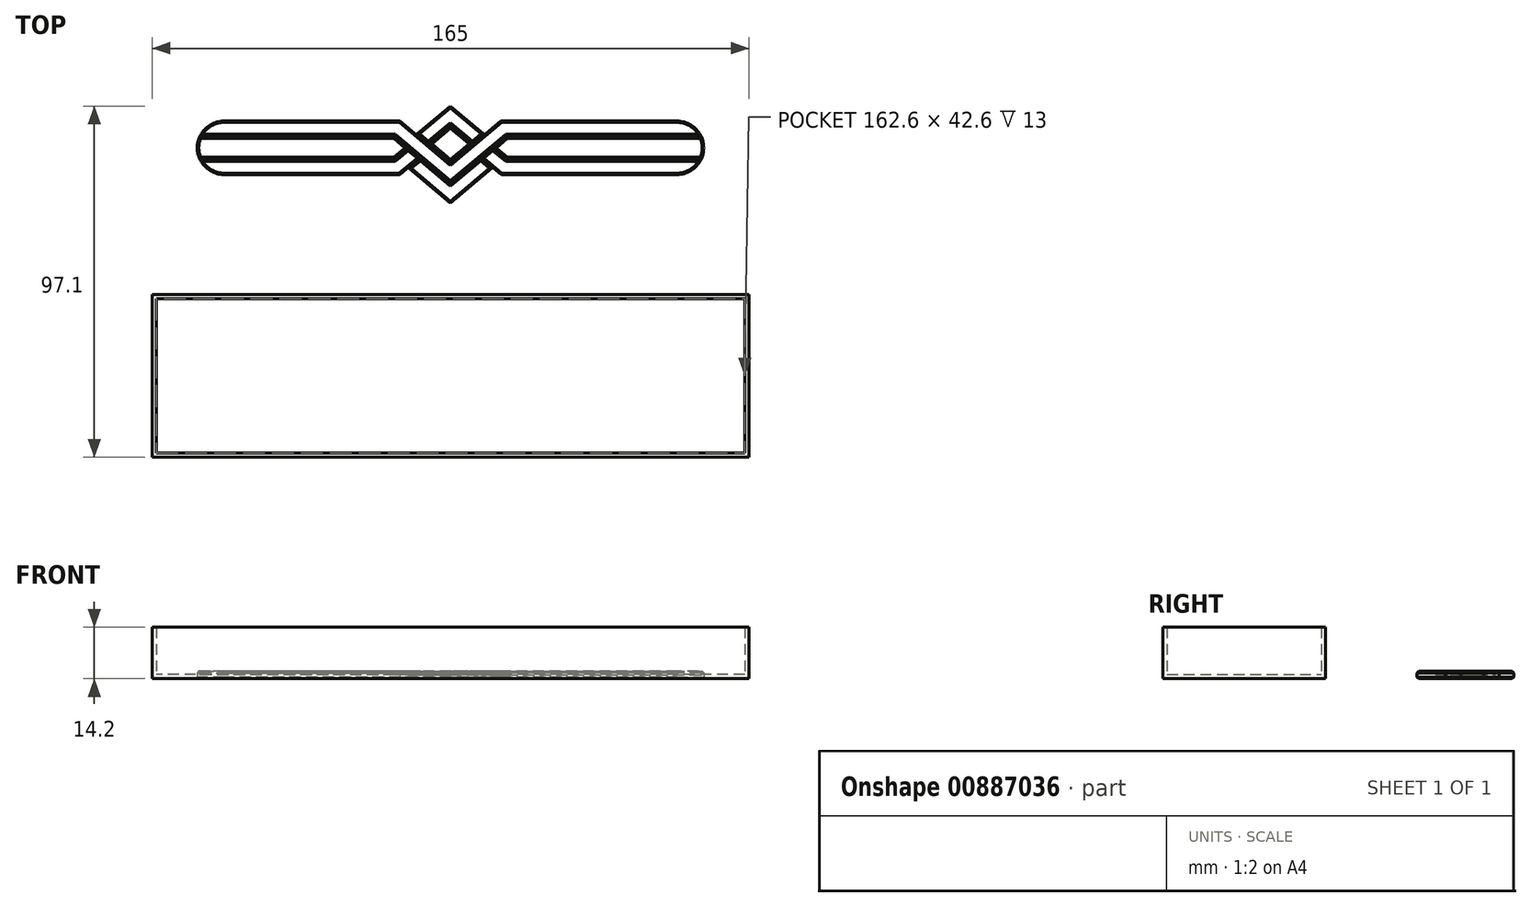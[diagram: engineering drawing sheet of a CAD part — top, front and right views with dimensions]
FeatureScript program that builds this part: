
annotation { "Feature Type Name" : "Feature", "Feature Type Description" : "" }
export const myFeature = defineFeature(function(context is Context, id is Id, definition is map)
    precondition{}
    {
        {
            var Q0;
            Q0=qCreatedBy(makeId("Top.planeOp"),FACE);
            var sketch = newSketch(context, id + "F0", { "sketchPlane" : qUnion([Q0])});
            skLineSegment(sketch, "E0", {"start": v(12, 0) * mm, "end": v(15.58, 3) * mm});
            skLineSegment(sketch, "E1", {"start": v(15.58, 3) * mm, "end": v(70, 3) * mm});
            skLineSegment(sketch, "E2", {"start": v(70, 3) * mm, "end": v(70, 0) * mm});
            skLineSegment(sketch, "E3.MirrorCS", {"start": v(12, 0) * mm, "end": v(15.58, -3) * mm});
            skLineSegment(sketch, "E4.MirrorCS", {"start": v(15.58, -3) * mm, "end": v(70, -3) * mm});
            skLineSegment(sketch, "E5.MirrorCS", {"start": v(70, -3) * mm, "end": v(70, 0) * mm});
            skLineSegment(sketch, "E6.MirrorCS", {"start": v(-12, 0) * mm, "end": v(-15.58, 3) * mm});
            skLineSegment(sketch, "E7.MirrorCS", {"start": v(-15.58, -3) * mm, "end": v(-70, -3) * mm});
            skLineSegment(sketch, "E8.MirrorCS", {"start": v(-12, 0) * mm, "end": v(-15.58, -3) * mm});
            skLineSegment(sketch, "E9.MirrorCS", {"start": v(-15.58, 3) * mm, "end": v(-70, 3) * mm});
            skLineSegment(sketch, "E10.MirrorCS", {"start": v(-70, -3) * mm, "end": v(-70, 0) * mm});
            skLineSegment(sketch, "E11.MirrorCS", {"start": v(-70, 3) * mm, "end": v(-70, 0) * mm});
            skSolve(sketch);
        }
        {
            var Q0;
            Q0=qSketchRegion(id+"F0",true);
            extrude(context, id + "F1", {"entities" : qUnion([Q0]), "depth" : 2 * mm, "offsetDistance" : 25 * mm});
        }
        {
            var Q0;
            Q0=qCreatedBy(makeId("Top.planeOp"),FACE);
            var sketch = newSketch(context, id + "F2", { "sketchPlane" : qUnion([Q0])});
            skLineSegment(sketch, "E12", {"start": v(0, -9.55) * mm, "end": v(15.43, 3.4) * mm});
            skLineSegment(sketch, "E13", {"start": v(15.43, 3.4) * mm, "end": v(70, 3.4) * mm});
            skLineSegment(sketch, "E14", {"start": v(70, 3.4) * mm, "end": v(70, 7.4) * mm});
            skLineSegment(sketch, "E15", {"start": v(70, 7.4) * mm, "end": v(13.97, 7.4) * mm});
            skLineSegment(sketch, "E16", {"start": v(13.97, 7.4) * mm, "end": v(0, -4.33) * mm});
            skLineSegment(sketch, "E17.MirrorCS", {"start": v(-70, 3.4) * mm, "end": v(-70, 7.4) * mm});
            skLineSegment(sketch, "E18.MirrorCS", {"start": v(-70, 7.4) * mm, "end": v(-13.97, 7.4) * mm});
            skLineSegment(sketch, "E19.MirrorCS", {"start": v(0, -9.55) * mm, "end": v(-15.43, 3.4) * mm});
            skLineSegment(sketch, "E20.MirrorCS", {"start": v(-13.97, 7.4) * mm, "end": v(0, -4.33) * mm});
            skLineSegment(sketch, "E21.MirrorCS", {"start": v(-15.43, 3.4) * mm, "end": v(-70, 3.4) * mm});
            skSolve(sketch);
        }
        {
            var Q0;
            Q0=qSketchRegion(id+"F2",true);
            extrude(context, id + "F3", {"entities" : qUnion([Q0]), "depth" : 2 * mm, "offsetDistance" : 25 * mm});
        }
        {
            var Q0;
            Q0=qCreatedBy(makeId("Top.planeOp"),FACE);
            var sketch = newSketch(context, id + "F4", { "sketchPlane" : qUnion([Q0])});
            skLineSegment(sketch, "E22", {"start": v(9.14, 3.87) * mm, "end": v(6.08, 1.3) * mm});
            skLineSegment(sketch, "E23", {"start": v(6.08, 1.3) * mm, "end": v(0, 6.4) * mm});
            skLineSegment(sketch, "E24", {"start": v(9.14, 3.87) * mm, "end": v(0, 11.54) * mm});
            skLineSegment(sketch, "E25", {"start": v(11.69, -0.26) * mm, "end": v(15.43, -3.4) * mm});
            skLineSegment(sketch, "E26", {"start": v(15.43, -3.4) * mm, "end": v(70, -3.4) * mm});
            skLineSegment(sketch, "E27", {"start": v(70, -3.4) * mm, "end": v(70, -7.4) * mm});
            skLineSegment(sketch, "E28", {"start": v(70, -7.4) * mm, "end": v(14.07, -7.4) * mm});
            skLineSegment(sketch, "E29", {"start": v(14.07, -7.4) * mm, "end": v(8.62, -2.83) * mm});
            skLineSegment(sketch, "E30", {"start": v(8.62, -2.83) * mm, "end": v(11.69, -0.26) * mm});
            skLineSegment(sketch, "E31.MirrorCS", {"start": v(-9.14, 3.87) * mm, "end": v(-6.08, 1.3) * mm});
            skLineSegment(sketch, "E32.MirrorCS", {"start": v(-9.14, 3.87) * mm, "end": v(0, 11.54) * mm});
            skLineSegment(sketch, "E33.MirrorCS", {"start": v(-6.08, 1.3) * mm, "end": v(0, 6.4) * mm});
            skLineSegment(sketch, "E34.MirrorCS", {"start": v(-14.07, -7.4) * mm, "end": v(-8.62, -2.83) * mm});
            skLineSegment(sketch, "E35.MirrorCS", {"start": v(-11.69, -0.26) * mm, "end": v(-15.43, -3.4) * mm});
            skLineSegment(sketch, "E36.MirrorCS", {"start": v(-70, -7.4) * mm, "end": v(-14.07, -7.4) * mm});
            skLineSegment(sketch, "E37.MirrorCS", {"start": v(-8.62, -2.83) * mm, "end": v(-11.69, -0.26) * mm});
            skLineSegment(sketch, "E38.MirrorCS", {"start": v(-15.43, -3.4) * mm, "end": v(-70, -3.4) * mm});
            skLineSegment(sketch, "E39.MirrorCS", {"start": v(-70, -3.4) * mm, "end": v(-70, -7.4) * mm});
            skSolve(sketch);
        }
        {
            var Q0;
            Q0=qSketchRegion(id+"F4",true);
            extrude(context, id + "F5", {"entities" : qUnion([Q0]), "depth" : 2 * mm, "offsetDistance" : 25 * mm});
        }
        {
            var Q0;
            Q0=qCreatedBy(makeId("Top.planeOp"),FACE);
            var sketch = newSketch(context, id + "F6", { "sketchPlane" : qUnion([Q0])});
            skLineSegment(sketch, "E40", {"start": v(0, -15.3) * mm, "end": v(11.42, -5.7) * mm});
            skLineSegment(sketch, "E41", {"start": v(11.42, -5.7) * mm, "end": v(8.31, -3.1) * mm});
            skLineSegment(sketch, "E42", {"start": v(8.31, -3.1) * mm, "end": v(0, -10.07) * mm});
            skLineSegment(sketch, "E43", {"start": v(0, -3.8) * mm, "end": v(5.77, 1.04) * mm});
            skLineSegment(sketch, "E44", {"start": v(5.77, 1.04) * mm, "end": v(0, 5.88) * mm});
            skLineSegment(sketch, "E45.MirrorCS", {"start": v(-5.77, 1.04) * mm, "end": v(0, 5.88) * mm});
            skLineSegment(sketch, "E46.MirrorCS", {"start": v(0, -15.3) * mm, "end": v(-11.42, -5.7) * mm});
            skLineSegment(sketch, "E47.MirrorCS", {"start": v(0, -3.8) * mm, "end": v(-5.77, 1.04) * mm});
            skLineSegment(sketch, "E48.MirrorCS", {"start": v(-11.42, -5.7) * mm, "end": v(-8.31, -3.1) * mm});
            skLineSegment(sketch, "E49.MirrorCS", {"start": v(-8.31, -3.1) * mm, "end": v(0, -10.07) * mm});
            skSolve(sketch);
        }
        {
            var Q0;
            Q0=qSketchRegion(id+"F6",true);
            extrude(context, id + "F7", {"entities" : qUnion([Q0]), "depth" : 2 * mm, "offsetDistance" : 25 * mm});
        }
        {
            var Q0;
            Q0=qCreatedBy(makeId("Top.planeOp"),FACE);
            var sketch = newSketch(context, id + "F8", { "sketchPlane" : qUnion([Q0])});
            skLineSegment(sketch, "E50", {"start": v(0, 11.54) * mm, "end": v(9.46, 3.6) * mm});
            skLineSegment(sketch, "E51", {"start": v(9.46, 3.6) * mm, "end": v(13.97, 7.4) * mm});
            skLineSegment(sketch, "E52", {"start": v(13.97, 7.4) * mm, "end": v(70, 7.4) * mm});
            skLineSegment(sketch, "E53", {"start": v(70, 7.4) * mm, "end": v(70, -7.4) * mm});
            skLineSegment(sketch, "E54", {"start": v(70, -7.4) * mm, "end": v(14.07, -7.4) * mm});
            skLineSegment(sketch, "E55", {"start": v(14.07, -7.4) * mm, "end": v(11.74, -5.44) * mm});
            skLineSegment(sketch, "E56", {"start": v(11.74, -5.44) * mm, "end": v(0, -15.3) * mm});
            skLineSegment(sketch, "E57.MirrorCS", {"start": v(-70, 7.4) * mm, "end": v(-70, -7.4) * mm});
            skLineSegment(sketch, "E58.MirrorCS", {"start": v(0, 11.54) * mm, "end": v(-9.46, 3.6) * mm});
            skLineSegment(sketch, "E59.MirrorCS", {"start": v(-13.97, 7.4) * mm, "end": v(-70, 7.4) * mm});
            skLineSegment(sketch, "E60.MirrorCS", {"start": v(-70, -7.4) * mm, "end": v(-14.07, -7.4) * mm});
            skLineSegment(sketch, "E61.MirrorCS", {"start": v(-14.07, -7.4) * mm, "end": v(-11.74, -5.44) * mm});
            skLineSegment(sketch, "E62.MirrorCS", {"start": v(-9.46, 3.6) * mm, "end": v(-13.97, 7.4) * mm});
            skLineSegment(sketch, "E63.MirrorCS", {"start": v(-11.74, -5.44) * mm, "end": v(0, -15.3) * mm});
            skSolve(sketch);
        }
        {
            var Q0;
            Q0=qSketchRegion(id+"F8",true);
            extrude(context, id + "F9", {"entities" : qUnion([Q0]), "depth" : 1 * mm, "offsetDistance" : 25 * mm});
        }
        {
            var Q0;
            Q0=makeQuery(id+"F1.opExtrude","SWEPT_BODY",BODY,{"disambiguationData":[OSD([sQuery(id+"F0.wireOp",EDGE,"E0"),sQuery(id+"F0.wireOp",EDGE,"E1"),sQuery(id+"F0.wireOp",EDGE,"E2"),sQuery(id+"F0.wireOp",EDGE,"E3.MirrorCS"),sQuery(id+"F0.wireOp",EDGE,"E4.MirrorCS"),sQuery(id+"F0.wireOp",EDGE,"E5.MirrorCS")])]});
            var Q1;
            Q1=makeQuery(id+"F1.opExtrude","SWEPT_BODY",BODY,{"disambiguationData":[OSD([sQuery(id+"F0.wireOp",EDGE,"E6.MirrorCS"),sQuery(id+"F0.wireOp",EDGE,"E7.MirrorCS"),sQuery(id+"F0.wireOp",EDGE,"E8.MirrorCS"),sQuery(id+"F0.wireOp",EDGE,"E9.MirrorCS"),sQuery(id+"F0.wireOp",EDGE,"E10.MirrorCS"),sQuery(id+"F0.wireOp",EDGE,"E11.MirrorCS")])]});
            var Q2;
            Q2=makeQuery(id+"F3.opExtrude","SWEPT_BODY",BODY,{"disambiguationData":[OSD([sQuery(id+"F2.wireOp",EDGE,"E12"),sQuery(id+"F2.wireOp",EDGE,"E13"),sQuery(id+"F2.wireOp",EDGE,"E14"),sQuery(id+"F2.wireOp",EDGE,"E15"),sQuery(id+"F2.wireOp",EDGE,"E16"),sQuery(id+"F2.wireOp",EDGE,"E17.MirrorCS"),sQuery(id+"F2.wireOp",EDGE,"E18.MirrorCS"),sQuery(id+"F2.wireOp",EDGE,"E19.MirrorCS"),sQuery(id+"F2.wireOp",EDGE,"E20.MirrorCS"),sQuery(id+"F2.wireOp",EDGE,"E21.MirrorCS")])]});
            var Q3;
            Q3=makeQuery(id+"F5.opExtrude","SWEPT_BODY",BODY,{"disambiguationData":[OSD([sQuery(id+"F4.wireOp",EDGE,"E22"),sQuery(id+"F4.wireOp",EDGE,"E23"),sQuery(id+"F4.wireOp",EDGE,"E24"),sQuery(id+"F4.wireOp",EDGE,"E31.MirrorCS"),sQuery(id+"F4.wireOp",EDGE,"E32.MirrorCS"),sQuery(id+"F4.wireOp",EDGE,"E33.MirrorCS")])]});
            var Q4;
            Q4=makeQuery(id+"F5.opExtrude","SWEPT_BODY",BODY,{"disambiguationData":[OSD([sQuery(id+"F4.wireOp",EDGE,"E25"),sQuery(id+"F4.wireOp",EDGE,"E26"),sQuery(id+"F4.wireOp",EDGE,"E27"),sQuery(id+"F4.wireOp",EDGE,"E28"),sQuery(id+"F4.wireOp",EDGE,"E29"),sQuery(id+"F4.wireOp",EDGE,"E30")])]});
            var Q5;
            Q5=makeQuery(id+"F5.opExtrude","SWEPT_BODY",BODY,{"disambiguationData":[OSD([sQuery(id+"F4.wireOp",EDGE,"E34.MirrorCS"),sQuery(id+"F4.wireOp",EDGE,"E35.MirrorCS"),sQuery(id+"F4.wireOp",EDGE,"E36.MirrorCS"),sQuery(id+"F4.wireOp",EDGE,"E37.MirrorCS"),sQuery(id+"F4.wireOp",EDGE,"E38.MirrorCS"),sQuery(id+"F4.wireOp",EDGE,"E39.MirrorCS")])]});
            var Q6;
            Q6=makeQuery(id+"F7.opExtrude","SWEPT_BODY",BODY,{"disambiguationData":[OSD([sQuery(id+"F6.wireOp",EDGE,"E40"),sQuery(id+"F6.wireOp",EDGE,"E41"),sQuery(id+"F6.wireOp",EDGE,"E42"),sQuery(id+"F6.wireOp",EDGE,"E46.MirrorCS"),sQuery(id+"F6.wireOp",EDGE,"E48.MirrorCS"),sQuery(id+"F6.wireOp",EDGE,"E49.MirrorCS")])]});
            var Q7;
            Q7=makeQuery(id+"F7.opExtrude","SWEPT_BODY",BODY,{"disambiguationData":[OSD([sQuery(id+"F6.wireOp",EDGE,"E43"),sQuery(id+"F6.wireOp",EDGE,"E44"),sQuery(id+"F6.wireOp",EDGE,"E45.MirrorCS"),sQuery(id+"F6.wireOp",EDGE,"E47.MirrorCS")])]});
            var Q8;
            Q8=makeQuery(id+"F9.opExtrude","SWEPT_BODY",BODY,{"disambiguationData":[OSD([sQuery(id+"F8.wireOp",EDGE,"E50"),sQuery(id+"F8.wireOp",EDGE,"E51"),sQuery(id+"F8.wireOp",EDGE,"E52"),sQuery(id+"F8.wireOp",EDGE,"E53"),sQuery(id+"F8.wireOp",EDGE,"E54"),sQuery(id+"F8.wireOp",EDGE,"E55"),sQuery(id+"F8.wireOp",EDGE,"E56"),sQuery(id+"F8.wireOp",EDGE,"E57.MirrorCS"),sQuery(id+"F8.wireOp",EDGE,"E58.MirrorCS"),sQuery(id+"F8.wireOp",EDGE,"E59.MirrorCS"),sQuery(id+"F8.wireOp",EDGE,"E60.MirrorCS"),sQuery(id+"F8.wireOp",EDGE,"E61.MirrorCS"),sQuery(id+"F8.wireOp",EDGE,"E62.MirrorCS"),sQuery(id+"F8.wireOp",EDGE,"E63.MirrorCS")])]});
            booleanBodies(context, id + "F10", {"operationType" : BooleanOperationType.UNION, "tools" : qUnion([Q0, Q1, Q2, Q3, Q4, Q5, Q6, Q7, Q8])});
        }
        {
            var Q0;
            Q0=qCreatedBy(makeId("Top.planeOp"),FACE);
            var sketch = newSketch(context, id + "F11", { "sketchPlane" : qUnion([Q0])});
            skArc(sketch, "E64", {"start": v(62.6, -7.4) * mm, "mid": v(70, 0) * mm, "end": v(62.6, 7.4) * mm});
            skLineSegment(sketch, "E65", {"start": v(62.6, 7.4) * mm, "end": v(112.12, 7.4) * mm});
            skLineSegment(sketch, "E66", {"start": v(112.12, 7.4) * mm, "end": v(112.12, -7.4) * mm});
            skLineSegment(sketch, "E67", {"start": v(62.6, -7.4) * mm, "end": v(112.12, -7.4) * mm});
            skArc(sketch, "E68.MirrorCS", {"start": v(-62.6, -7.4) * mm, "mid": v(-70, 0) * mm, "end": v(-62.6, 7.4) * mm});
            skLineSegment(sketch, "E69.MirrorCS", {"start": v(-62.6, -7.4) * mm, "end": v(-112.12, -7.4) * mm});
            skLineSegment(sketch, "E70.MirrorCS", {"start": v(-62.6, 7.4) * mm, "end": v(-112.12, 7.4) * mm});
            skLineSegment(sketch, "E71.MirrorCS", {"start": v(-112.12, 7.4) * mm, "end": v(-112.12, -7.4) * mm});
            skSolve(sketch);
        }
        {
            var Q0;
            Q0=qSketchRegion(id+"F11",true);
            var Q1;
            Q1=makeQuery(id+"F1.opExtrude","CAP_FACE",FACE,{"disambiguationData":[OSD([sQuery(id+"F0.wireOp",EDGE,"E0"),sQuery(id+"F0.wireOp",EDGE,"E1"),sQuery(id+"F0.wireOp",EDGE,"E2"),sQuery(id+"F0.wireOp",EDGE,"E3.MirrorCS"),sQuery(id+"F0.wireOp",EDGE,"E4.MirrorCS"),sQuery(id+"F0.wireOp",EDGE,"E5.MirrorCS")])],"isStart":false});
            extrude(context, id + "F12", {"entities" : qUnion([Q0]), "operationType" : NewBodyOperationType.REMOVE, "endBound" : BoundingType.UP_TO_SURFACE, "depth" : 12.5 * mm, "endBoundEntityFace" : qUnion([Q1]), "offsetDistance" : 25 * mm});
        }
        {
            var Q0;
            Q0=makeQuery(id+"F3.opExtrude","CAP_FACE",FACE,{"disambiguationData":[OSD([sQuery(id+"F2.wireOp",EDGE,"E12"),sQuery(id+"F2.wireOp",EDGE,"E13"),sQuery(id+"F2.wireOp",EDGE,"E14"),sQuery(id+"F2.wireOp",EDGE,"E15"),sQuery(id+"F2.wireOp",EDGE,"E16"),sQuery(id+"F2.wireOp",EDGE,"E17.MirrorCS"),sQuery(id+"F2.wireOp",EDGE,"E18.MirrorCS"),sQuery(id+"F2.wireOp",EDGE,"E19.MirrorCS"),sQuery(id+"F2.wireOp",EDGE,"E20.MirrorCS"),sQuery(id+"F2.wireOp",EDGE,"E21.MirrorCS")])],"isStart":false});
            var Q1;
            Q1=makeQuery(id+"F1.opExtrude","CAP_FACE",FACE,{"disambiguationData":[OSD([sQuery(id+"F0.wireOp",EDGE,"E6.MirrorCS"),sQuery(id+"F0.wireOp",EDGE,"E7.MirrorCS"),sQuery(id+"F0.wireOp",EDGE,"E8.MirrorCS"),sQuery(id+"F0.wireOp",EDGE,"E9.MirrorCS"),sQuery(id+"F0.wireOp",EDGE,"E10.MirrorCS"),sQuery(id+"F0.wireOp",EDGE,"E11.MirrorCS")])],"isStart":false});
            var Q2;
            Q2=makeQuery(id+"F5.opExtrude","CAP_FACE",FACE,{"disambiguationData":[OSD([sQuery(id+"F4.wireOp",EDGE,"E34.MirrorCS"),sQuery(id+"F4.wireOp",EDGE,"E35.MirrorCS"),sQuery(id+"F4.wireOp",EDGE,"E36.MirrorCS"),sQuery(id+"F4.wireOp",EDGE,"E37.MirrorCS"),sQuery(id+"F4.wireOp",EDGE,"E38.MirrorCS"),sQuery(id+"F4.wireOp",EDGE,"E39.MirrorCS")])],"isStart":false});
            var Q3;
            Q3=makeQuery(id+"F5.opExtrude","CAP_FACE",FACE,{"disambiguationData":[OSD([sQuery(id+"F4.wireOp",EDGE,"E22"),sQuery(id+"F4.wireOp",EDGE,"E23"),sQuery(id+"F4.wireOp",EDGE,"E24"),sQuery(id+"F4.wireOp",EDGE,"E31.MirrorCS"),sQuery(id+"F4.wireOp",EDGE,"E32.MirrorCS"),sQuery(id+"F4.wireOp",EDGE,"E33.MirrorCS")])],"isStart":false});
            var Q4;
            Q4=makeQuery(id+"F7.opExtrude","CAP_FACE",FACE,{"disambiguationData":[OSD([sQuery(id+"F6.wireOp",EDGE,"E43"),sQuery(id+"F6.wireOp",EDGE,"E44"),sQuery(id+"F6.wireOp",EDGE,"E45.MirrorCS"),sQuery(id+"F6.wireOp",EDGE,"E47.MirrorCS")])],"isStart":false});
            var Q5;
            Q5=makeQuery(id+"F7.opExtrude","CAP_FACE",FACE,{"disambiguationData":[OSD([sQuery(id+"F6.wireOp",EDGE,"E40"),sQuery(id+"F6.wireOp",EDGE,"E41"),sQuery(id+"F6.wireOp",EDGE,"E42"),sQuery(id+"F6.wireOp",EDGE,"E46.MirrorCS"),sQuery(id+"F6.wireOp",EDGE,"E48.MirrorCS"),sQuery(id+"F6.wireOp",EDGE,"E49.MirrorCS")])],"isStart":false});
            var Q6;
            Q6=makeQuery(id+"F5.opExtrude","CAP_FACE",FACE,{"disambiguationData":[OSD([sQuery(id+"F4.wireOp",EDGE,"E25"),sQuery(id+"F4.wireOp",EDGE,"E26"),sQuery(id+"F4.wireOp",EDGE,"E27"),sQuery(id+"F4.wireOp",EDGE,"E28"),sQuery(id+"F4.wireOp",EDGE,"E29"),sQuery(id+"F4.wireOp",EDGE,"E30")])],"isStart":false});
            var Q7;
            Q7=makeQuery(id+"F1.opExtrude","CAP_FACE",FACE,{"disambiguationData":[OSD([sQuery(id+"F0.wireOp",EDGE,"E0"),sQuery(id+"F0.wireOp",EDGE,"E1"),sQuery(id+"F0.wireOp",EDGE,"E2"),sQuery(id+"F0.wireOp",EDGE,"E3.MirrorCS"),sQuery(id+"F0.wireOp",EDGE,"E4.MirrorCS"),sQuery(id+"F0.wireOp",EDGE,"E5.MirrorCS")])],"isStart":false});
            var Q8;
            Q8=makeQuery(id+"F10.opBoolean","MERGE",FACE,{"derivedFrom":[makeQuery(id+"F1.opExtrude","CAP_FACE",FACE,{"disambiguationData":[OSD([sQuery(id+"F0.wireOp",EDGE,"E0"),sQuery(id+"F0.wireOp",EDGE,"E1"),sQuery(id+"F0.wireOp",EDGE,"E2"),sQuery(id+"F0.wireOp",EDGE,"E3.MirrorCS"),sQuery(id+"F0.wireOp",EDGE,"E4.MirrorCS"),sQuery(id+"F0.wireOp",EDGE,"E5.MirrorCS")])],"isStart":true}),makeQuery(id+"F1.opExtrude","CAP_FACE",FACE,{"disambiguationData":[OSD([sQuery(id+"F0.wireOp",EDGE,"E6.MirrorCS"),sQuery(id+"F0.wireOp",EDGE,"E7.MirrorCS"),sQuery(id+"F0.wireOp",EDGE,"E8.MirrorCS"),sQuery(id+"F0.wireOp",EDGE,"E9.MirrorCS"),sQuery(id+"F0.wireOp",EDGE,"E10.MirrorCS"),sQuery(id+"F0.wireOp",EDGE,"E11.MirrorCS")])],"isStart":true}),makeQuery(id+"F3.opExtrude","CAP_FACE",FACE,{"disambiguationData":[OSD([sQuery(id+"F2.wireOp",EDGE,"E12"),sQuery(id+"F2.wireOp",EDGE,"E13"),sQuery(id+"F2.wireOp",EDGE,"E14"),sQuery(id+"F2.wireOp",EDGE,"E15"),sQuery(id+"F2.wireOp",EDGE,"E16"),sQuery(id+"F2.wireOp",EDGE,"E17.MirrorCS"),sQuery(id+"F2.wireOp",EDGE,"E18.MirrorCS"),sQuery(id+"F2.wireOp",EDGE,"E19.MirrorCS"),sQuery(id+"F2.wireOp",EDGE,"E20.MirrorCS"),sQuery(id+"F2.wireOp",EDGE,"E21.MirrorCS")])],"isStart":true}),makeQuery(id+"F5.opExtrude","CAP_FACE",FACE,{"disambiguationData":[OSD([sQuery(id+"F4.wireOp",EDGE,"E22"),sQuery(id+"F4.wireOp",EDGE,"E23"),sQuery(id+"F4.wireOp",EDGE,"E24"),sQuery(id+"F4.wireOp",EDGE,"E31.MirrorCS"),sQuery(id+"F4.wireOp",EDGE,"E32.MirrorCS"),sQuery(id+"F4.wireOp",EDGE,"E33.MirrorCS")])],"isStart":true}),makeQuery(id+"F5.opExtrude","CAP_FACE",FACE,{"disambiguationData":[OSD([sQuery(id+"F4.wireOp",EDGE,"E25"),sQuery(id+"F4.wireOp",EDGE,"E26"),sQuery(id+"F4.wireOp",EDGE,"E27"),sQuery(id+"F4.wireOp",EDGE,"E28"),sQuery(id+"F4.wireOp",EDGE,"E29"),sQuery(id+"F4.wireOp",EDGE,"E30")])],"isStart":true}),makeQuery(id+"F5.opExtrude","CAP_FACE",FACE,{"disambiguationData":[OSD([sQuery(id+"F4.wireOp",EDGE,"E34.MirrorCS"),sQuery(id+"F4.wireOp",EDGE,"E35.MirrorCS"),sQuery(id+"F4.wireOp",EDGE,"E36.MirrorCS"),sQuery(id+"F4.wireOp",EDGE,"E37.MirrorCS"),sQuery(id+"F4.wireOp",EDGE,"E38.MirrorCS"),sQuery(id+"F4.wireOp",EDGE,"E39.MirrorCS")])],"isStart":true}),makeQuery(id+"F7.opExtrude","CAP_FACE",FACE,{"disambiguationData":[OSD([sQuery(id+"F6.wireOp",EDGE,"E40"),sQuery(id+"F6.wireOp",EDGE,"E41"),sQuery(id+"F6.wireOp",EDGE,"E42"),sQuery(id+"F6.wireOp",EDGE,"E46.MirrorCS"),sQuery(id+"F6.wireOp",EDGE,"E48.MirrorCS"),sQuery(id+"F6.wireOp",EDGE,"E49.MirrorCS")])],"isStart":true}),makeQuery(id+"F7.opExtrude","CAP_FACE",FACE,{"disambiguationData":[OSD([sQuery(id+"F6.wireOp",EDGE,"E43"),sQuery(id+"F6.wireOp",EDGE,"E44"),sQuery(id+"F6.wireOp",EDGE,"E45.MirrorCS"),sQuery(id+"F6.wireOp",EDGE,"E47.MirrorCS")])],"isStart":true}),makeQuery(id+"F9.opExtrude","CAP_FACE",FACE,{"disambiguationData":[OSD([sQuery(id+"F8.wireOp",EDGE,"E50"),sQuery(id+"F8.wireOp",EDGE,"E51"),sQuery(id+"F8.wireOp",EDGE,"E52"),sQuery(id+"F8.wireOp",EDGE,"E53"),sQuery(id+"F8.wireOp",EDGE,"E54"),sQuery(id+"F8.wireOp",EDGE,"E55"),sQuery(id+"F8.wireOp",EDGE,"E56"),sQuery(id+"F8.wireOp",EDGE,"E57.MirrorCS"),sQuery(id+"F8.wireOp",EDGE,"E58.MirrorCS"),sQuery(id+"F8.wireOp",EDGE,"E59.MirrorCS"),sQuery(id+"F8.wireOp",EDGE,"E60.MirrorCS"),sQuery(id+"F8.wireOp",EDGE,"E61.MirrorCS"),sQuery(id+"F8.wireOp",EDGE,"E62.MirrorCS"),sQuery(id+"F8.wireOp",EDGE,"E63.MirrorCS")])],"isStart":true})]});
            chamfer(context, id + "F13", {"entities" : qUnion([Q0, Q1, Q2, Q3, Q4, Q5, Q6, Q7, Q8]), "width" : 0.4 * mm, "tangentPropagation" : true});
        }
        {
            var Q0;
            Q0=qCreatedBy(makeId("Top.planeOp"),FACE);
            var sketch = newSketch(context, id + "F14", { "sketchPlane" : qUnion([Q0])});
            skLineSegment(sketch, "E72.bottom", {"start": v(82.5, -85.56) * mm, "end": v(-82.5, -85.56) * mm});
            skLineSegment(sketch, "E72.top", {"start": v(82.5, -40.56) * mm, "end": v(-82.5, -40.56) * mm});
            skLineSegment(sketch, "E72.left", {"start": v(82.5, -85.56) * mm, "end": v(82.5, -40.56) * mm});
            skLineSegment(sketch, "E72.right", {"start": v(-82.5, -85.56) * mm, "end": v(-82.5, -40.56) * mm});
            skPoint(sketch, "E72.middle", {"position": v(0, -63.06) * mm});
            skSolve(sketch);
        }
        {
            var Q0;
            Q0=makeQuery(id+"F14.imprint","IMPRINT",FACE,{"disambiguationData":[TD([[makeQuery(id+"F14.imprint","IMPRINT",EDGE,{"derivedFrom":sQuery(id+"F14.wireOp",EDGE,"E72.bottom")}),-1.0]])]});
            extrude(context, id + "F15", {"entities" : qUnion([Q0]), "depth" : 1.2 * mm, "offsetDistance" : 25 * mm});
        }
        {
            var Q0;
            Q0=makeQuery(id+"F15.opExtrude","CAP_FACE",FACE,{"disambiguationData":[OSD([sQuery(id+"F14.wireOp",EDGE,"E72.bottom"),sQuery(id+"F14.wireOp",EDGE,"E72.top"),sQuery(id+"F14.wireOp",EDGE,"E72.left"),sQuery(id+"F14.wireOp",EDGE,"E72.right")])],"isStart":false});
            var sketch = newSketch(context, id + "F16", { "sketchPlane" : qUnion([Q0])});
            skLineSegment(sketch, "E73.bottom", {"start": v(-82.5, -40.56) * mm, "end": v(82.5, -40.56) * mm});
            skLineSegment(sketch, "E73.top", {"start": v(-82.5, -85.56) * mm, "end": v(82.5, -85.56) * mm});
            skLineSegment(sketch, "E73.left", {"start": v(-82.5, -40.56) * mm, "end": v(-82.5, -85.56) * mm});
            skLineSegment(sketch, "E73.right", {"start": v(82.5, -40.56) * mm, "end": v(82.5, -85.56) * mm});
            skLineSegment(sketch, "E74.bottom", {"start": v(81.3, -84.36) * mm, "end": v(-81.3, -84.36) * mm});
            skLineSegment(sketch, "E74.top", {"start": v(81.3, -41.76) * mm, "end": v(-81.3, -41.76) * mm});
            skLineSegment(sketch, "E74.left", {"start": v(81.3, -84.36) * mm, "end": v(81.3, -41.76) * mm});
            skLineSegment(sketch, "E74.right", {"start": v(-81.3, -84.36) * mm, "end": v(-81.3, -41.76) * mm});
            skPoint(sketch, "E74.middle", {"position": v(0, -63.06) * mm});
            skPoint(sketch, "E74.middle.positionSnap0", {"position": v(82.5, -63.06) * mm});
            skPoint(sketch, "E74.middle.positionSnap1", {"position": v(0, -85.56) * mm});
            skPoint(sketch, "E74.centerSnap0", {"position": v(82.5, -63.06) * mm});
            skPoint(sketch, "E74.centerSnap1", {"position": v(0, -85.56) * mm});
            skSolve(sketch);
        }
        {
            var Q0;
            Q0=qSketchRegion(id+"F16",true);
            extrude(context, id + "F17", {"entities" : qUnion([Q0]), "operationType" : NewBodyOperationType.ADD, "depth" : 13 * mm, "offsetDistance" : 25 * mm});
        }
    });
